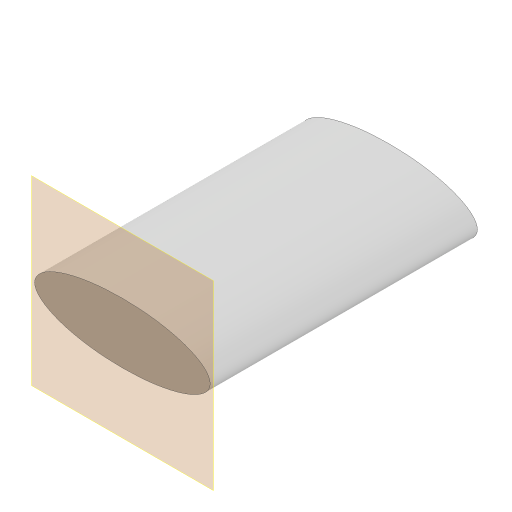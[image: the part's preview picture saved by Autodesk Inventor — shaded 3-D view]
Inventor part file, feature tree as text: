
AUTODESK INVENTOR PART (.ipt)
format: ipt  version: 2023 (Build 270158000, 158)  size: 90,624 bytes
history: native  units: in
note: dims shown in document units (in); Inventor stores cm internally (conversion verified against a paired STEP export)
features: other x3, plane x1, extrude x1, sketch x1
ambient origin geometry x8: Origin, YZ Plane, XZ Plane, XY Plane, X Axis, Y Axis, Z Axis, Center Point
bodies: Solid1 (feature_tree)
feature tree (6):
  plane  "Work Plane1"
  extrude  "Extrusion1"  [1 undecoded]
  sketch  "Sketch1"  dims[d0=118.1102in d1=0.0in]
  other  "<userpath>\vaRLnt\v3\demo\sigmaPoint\Assembly1.iam"
  other  "Assembly1.iam"
  other  "column:1"
note: 1 required parameter value undecoded (feature->parameter linkage not recoverable at this tier; creation-order binding heuristic only, values carry confidence <= 0.55)
